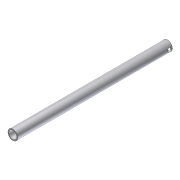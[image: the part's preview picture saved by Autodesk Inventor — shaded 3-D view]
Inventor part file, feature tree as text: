
AUTODESK INVENTOR PART (.ipt)
format: ipt  version: 2012 (Build 160160000, 160)  size: 79,360 bytes
history: native  units: in
note: dims shown in document units (in); Inventor stores cm internally (conversion verified against a paired STEP export)
features: extrude x2, sketch x2, shell x1, plane x1
ambient origin geometry x8: Origin, YZ Plane, XZ Plane, XY Plane, X Axis, Y Axis, Z Axis, Center Point
bodies: Solid1 (feature_tree)
feature tree (6):
  extrude  "Extrusion1"  Depth=20.5in TaperAngle=0.0deg
  shell  "Shell1"  Thickness=0.133in
  plane  "Work Plane1"
  extrude  "Extrusion2"  Depth=0.375in
  sketch  "Sketch1"  dims[d0=1.315in d1=20.5in d2=0.0in d3=0.133in]
  sketch  "Sketch3"  dims[d4=0.5in d5=0.375in d6=1.0in d7=0.0in]
